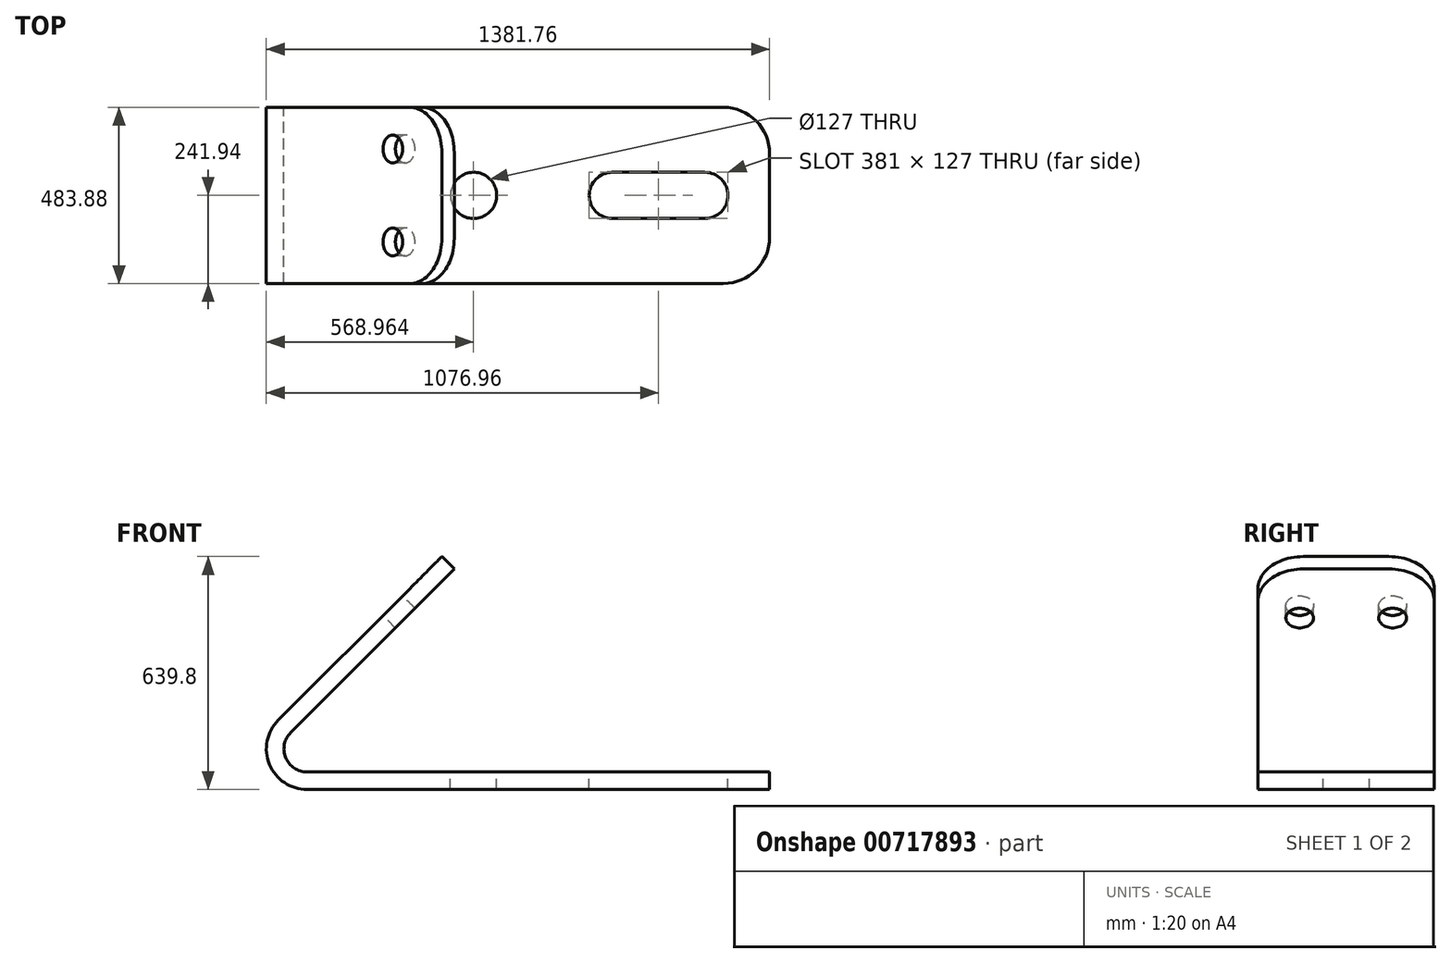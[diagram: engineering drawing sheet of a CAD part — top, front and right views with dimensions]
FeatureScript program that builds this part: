
annotation { "Feature Type Name" : "Feature", "Feature Type Description" : "" }
export const myFeature = defineFeature(function(context is Context, id is Id, definition is map)
    precondition{}
    {
        {
            var Q0;
            Q0=qCreatedBy(makeId("Front.planeOp"),FACE);
            var sketch = newSketch(context, id + "F0", { "sketchPlane" : qUnion([Q0])});
            skArc(sketch, "E0", {"start": v(-378.1, 44.9) * mm, "mid": v(-391.87, -24.3) * mm, "end": v(-333.2, -63.5) * mm});
            skArc(sketch, "E1", {"start": v(-412.23, 79.03) * mm, "mid": v(-436.46, -42.77) * mm, "end": v(-333.2, -111.76) * mm});
            skLineSegment(sketch, "E2", {"start": v(-333.2, -111.76) * mm, "end": v(936.8, -111.76) * mm});
            skLineSegment(sketch, "E3", {"start": v(-412.23, 79.03) * mm, "end": v(36.78, 528.04) * mm});
            skLineSegment(sketch, "E4", {"start": v(-378.1, 44.9) * mm, "end": v(70.9, 493.91) * mm});
            skLineSegment(sketch, "E5", {"start": v(-333.2, -63.5) * mm, "end": v(936.8, -63.5) * mm});
            skLineSegment(sketch, "E6", {"start": v(36.78, 528.04) * mm, "end": v(70.9, 493.91) * mm});
            skLineSegment(sketch, "E7", {"start": v(936.8, -63.5) * mm, "end": v(936.8, -111.76) * mm});
            skSolve(sketch);
        }
        {
            var Q0;
            Q0=makeQuery(id+"F0.imprint","IMPRINT",FACE,{"disambiguationData":[TD([[makeQuery(id+"F0.imprint","IMPRINT",EDGE,{"derivedFrom":sQuery(id+"F0.wireOp",EDGE,"E0")}),-1.0]])]});
            extrude(context, id + "F1", {"entities" : qUnion([Q0]), "endBound" : BoundingType.SYMMETRIC, "depth" : 483.87 * mm, "offsetDistance" : 25.4 * mm});
        }
        {
            var Q0;
            Q0=makeQuery(id+"F1.opExtrude","SWEPT_FACE",FACE,{"disambiguationData":[OSD([sQuery(id+"F0.wireOp",EDGE,"E3")])]});
            var sketch = newSketch(context, id + "F2", { "sketchPlane" : qUnion([Q0])});
            skLineSegment(sketch, "E8", {"start": v(127.64, -179.8) * mm, "end": v(127.64, 399.39) * mm, "construction": true});
            skLineSegment(sketch, "E9", {"start": v(-127.64, -179.8) * mm, "end": v(-127.64, 399.39) * mm, "construction": true});
            skLineSegment(sketch, "E10", {"start": v(-241.94, 208.89) * mm, "end": v(241.94, 208.89) * mm, "construction": true});
            skCircle(sketch, "E11", {"center": v(-127.64, 208.89) * mm, "radius": 38.1 * mm});
            skCircle(sketch, "E12", {"center": v(127.64, 208.89) * mm, "radius": 38.1 * mm});
            skSolve(sketch);
        }
        {
            var Q0;
            Q0=makeQuery(id+"F2.imprint","IMPRINT",FACE,{"disambiguationData":[TD([[makeQuery(id+"F2.imprint","IMPRINT",EDGE,{"derivedFrom":sQuery(id+"F2.wireOp",EDGE,"E12")}),1.0]])]});
            var Q1;
            Q1=makeQuery(id+"F2.imprint","IMPRINT",FACE,{"disambiguationData":[TD([[makeQuery(id+"F2.imprint","IMPRINT",EDGE,{"derivedFrom":sQuery(id+"F2.wireOp",EDGE,"E11")}),1.0]])]});
            extrude(context, id + "F3", {"entities" : qUnion([Q0, Q1]), "operationType" : NewBodyOperationType.REMOVE, "oppositeDirection" : true, "depth" : 157.23 * mm, "offsetDistance" : 25.4 * mm});
        }
        {
            var Q0;
            Q0=makeQuery(id+"F1.opExtrude","SWEPT_FACE",FACE,{"disambiguationData":[OSD([sQuery(id+"F0.wireOp",EDGE,"E5")])]});
            var sketch = newSketch(context, id + "F4", { "sketchPlane" : qUnion([Q0])});
            skCircle(sketch, "E13", {"center": v(124, 0) * mm, "radius": 63.5 * mm});
            skArc(sketch, "E14", {"start": v(505, 63.5) * mm, "mid": v(441.5, 0) * mm, "end": v(505, -63.5) * mm});
            skArc(sketch, "E15", {"start": v(759, -63.5) * mm, "mid": v(822.5, 0) * mm, "end": v(759, 63.5) * mm});
            skLineSegment(sketch, "E16", {"start": v(505, -63.5) * mm, "end": v(759, -63.5) * mm});
            skLineSegment(sketch, "E17", {"start": v(505, 63.5) * mm, "end": v(759, 63.5) * mm});
            skLineSegment(sketch, "E18.trimOffspring", {"start": v(187.5, 0) * mm, "end": v(124, 0) * mm, "construction": true});
            skPoint(sketch, "E19.start.orphan", {"position": v(936.8, 0) * mm});
            skSolve(sketch);
        }
        {
            var Q0;
            Q0=makeQuery(id+"F1.opExtrude","CAP_EDGE",EDGE,{"disambiguationData":[OSD([sQuery(id+"F0.wireOp",EDGE,"E6")])],"isStart":false});
            var Q1;
            Q1=makeQuery(id+"F1.opExtrude","CAP_EDGE",EDGE,{"disambiguationData":[OSD([sQuery(id+"F0.wireOp",EDGE,"E6")])],"isStart":true});
            fillet(context, id + "F5", {"entities" : qUnion([Q0, Q1]), "radius" : 124.46 * mm, "tangentPropagation" : true, "allowEdgeOverflow" : false});
        }
        {
            var Q0;
            Q0=makeQuery(id+"F1.opExtrude","CAP_EDGE",EDGE,{"disambiguationData":[OSD([sQuery(id+"F0.wireOp",EDGE,"E7")])],"isStart":true});
            var Q1;
            Q1=makeQuery(id+"F1.opExtrude","CAP_EDGE",EDGE,{"disambiguationData":[OSD([sQuery(id+"F0.wireOp",EDGE,"E7")])],"isStart":false});
            fillet(context, id + "F6", {"entities" : qUnion([Q0, Q1]), "radius" : 127 * mm, "tangentPropagation" : true, "allowEdgeOverflow" : false});
        }
        {
            var Q0;
            Q0=makeQuery(id+"F4.imprint","IMPRINT",FACE,{"disambiguationData":[TD([[makeQuery(id+"F4.imprint","IMPRINT",EDGE,{"derivedFrom":sQuery(id+"F4.wireOp",EDGE,"E13")}),1.0]])]});
            var Q1;
            Q1=makeQuery(id+"F4.imprint","IMPRINT",FACE,{"disambiguationData":[TD([[makeQuery(id+"F4.imprint","IMPRINT",EDGE,{"derivedFrom":sQuery(id+"F4.wireOp",EDGE,"E14")}),1.0]])]});
            extrude(context, id + "F7", {"entities" : qUnion([Q0, Q1]), "operationType" : NewBodyOperationType.REMOVE, "oppositeDirection" : true, "depth" : 1049.02 * mm, "offsetDistance" : 25.4 * mm});
        }
    });
